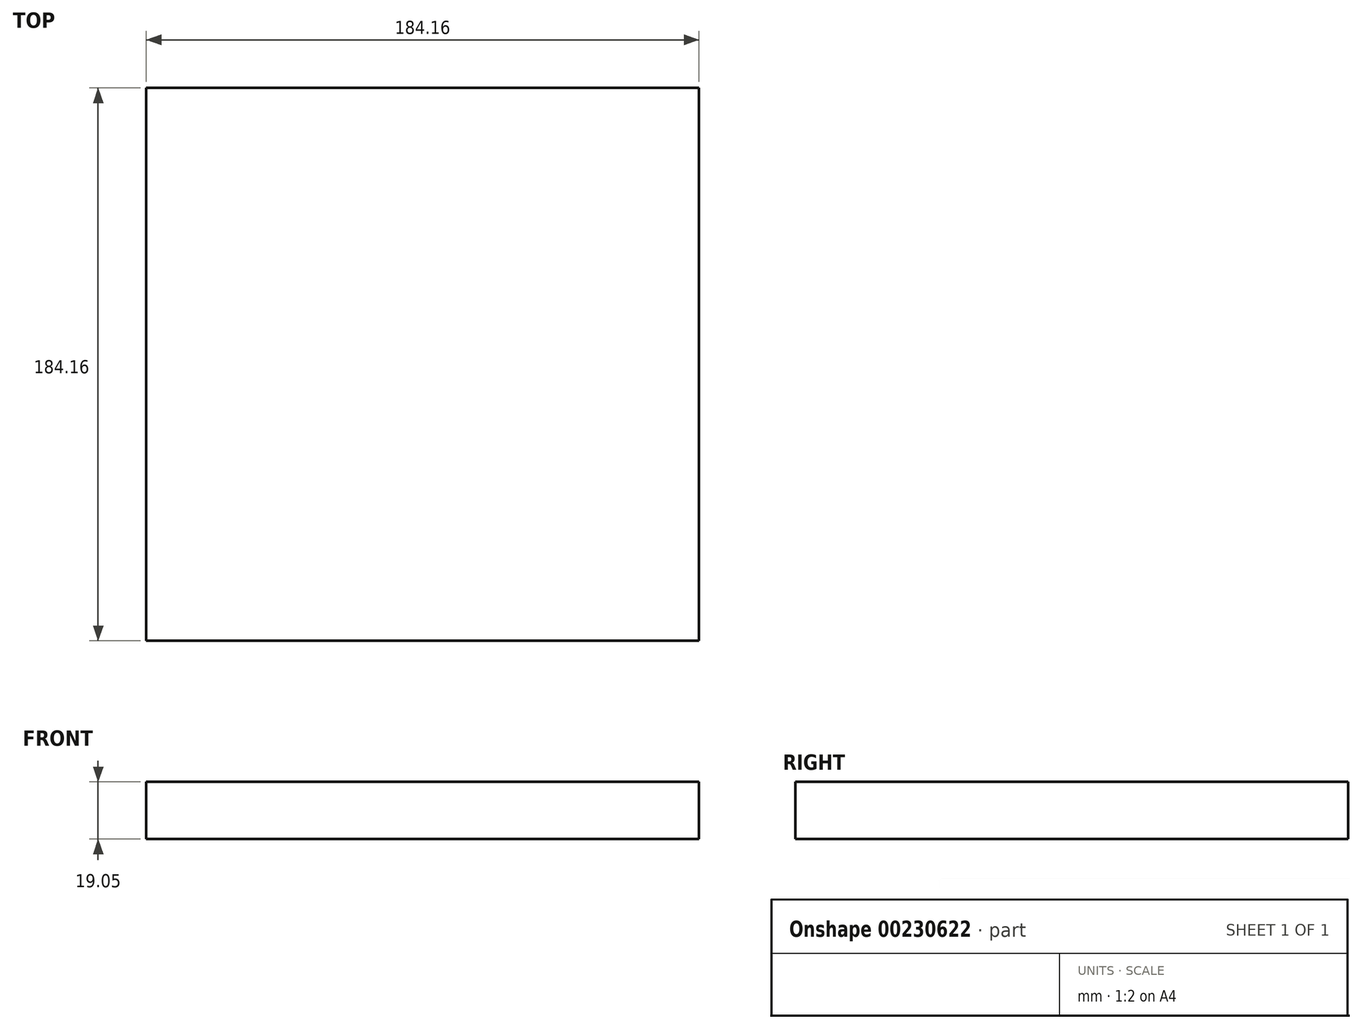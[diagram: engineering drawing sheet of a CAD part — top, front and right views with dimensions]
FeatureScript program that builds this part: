
annotation { "Feature Type Name" : "Feature", "Feature Type Description" : "" }
export const myFeature = defineFeature(function(context is Context, id is Id, definition is map)
    precondition{}
    {
        {
            var Q0;
            Q0=qCreatedBy(makeId("Top.planeOp"),FACE);
            var sketch = newSketch(context, id + "F0", { "sketchPlane" : qUnion([Q0])});
            skLineSegment(sketch, "E0.bottom", {"start": v(-92.07, 92.07) * mm, "end": v(92.08, 92.07) * mm});
            skLineSegment(sketch, "E0.top", {"start": v(-92.08, -92.08) * mm, "end": v(92.07, -92.08) * mm});
            skLineSegment(sketch, "E0.left", {"start": v(-92.07, 92.08) * mm, "end": v(-92.08, -92.07) * mm});
            skLineSegment(sketch, "E0.right", {"start": v(92.08, 92.07) * mm, "end": v(92.07, -92.08) * mm});
            skPoint(sketch, "E0.middle", {"position": v(0, 0) * mm});
            skSolve(sketch);
        }
        {
            var Q0;
            Q0 = qSketchRegion(id + "F0", true);
            extrude(context, id + "F1", {"entities" : qUnion([Q0]), "depth" : 19.05 * mm});
        }
    });
